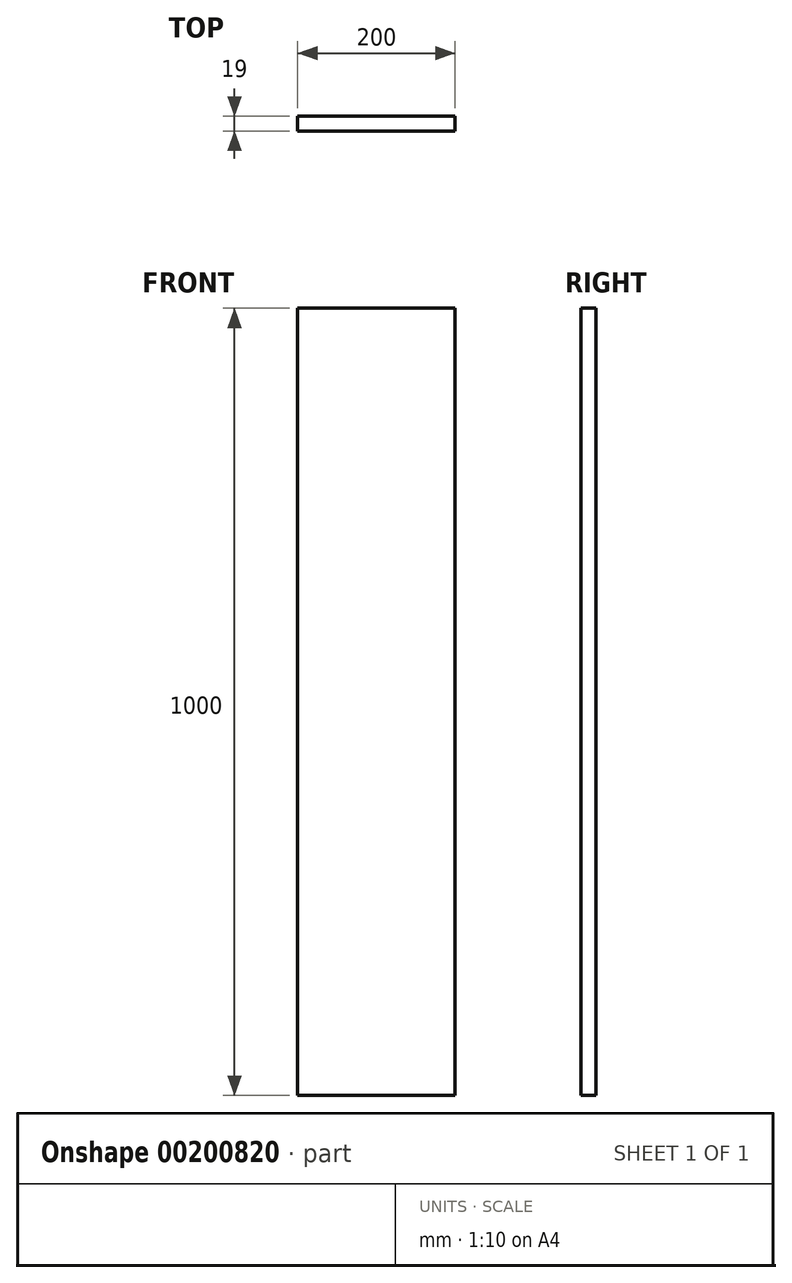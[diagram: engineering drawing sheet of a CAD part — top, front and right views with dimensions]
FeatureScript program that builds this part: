
annotation { "Feature Type Name" : "Feature", "Feature Type Description" : "" }
export const myFeature = defineFeature(function(context is Context, id is Id, definition is map)
    precondition{}
    {
        {
            var Q0;
            Q0=qCreatedBy(makeId("Front.planeOp"),FACE);
            var sketch = newSketch(context, id + "F0", { "sketchPlane" : qUnion([Q0])});
            skLineSegment(sketch, "E0.bottom", {"start": v(-98.72, 786.87) * mm, "end": v(101.28, 786.87) * mm});
            skLineSegment(sketch, "E0.top", {"start": v(-98.72, -213.13) * mm, "end": v(101.28, -213.13) * mm});
            skLineSegment(sketch, "E0.left", {"start": v(-98.72, 786.87) * mm, "end": v(-98.72, -213.13) * mm});
            skLineSegment(sketch, "E0.right", {"start": v(101.28, 786.87) * mm, "end": v(101.28, -213.13) * mm});
            skSolve(sketch);
        }
        {
            var Q0;
            Q0=makeQuery(id+"F0.imprint","IMPRINT",FACE,{"disambiguationData":[TD([[makeQuery(id+"F0.imprint","IMPRINT",EDGE,{"derivedFrom":sQuery(id+"F0.wireOp",EDGE,"E0.bottom")}),-1.0]])]});
            extrude(context, id + "F1", {"entities" : qUnion([Q0]), "depth" : 19 * mm});
        }
    });
